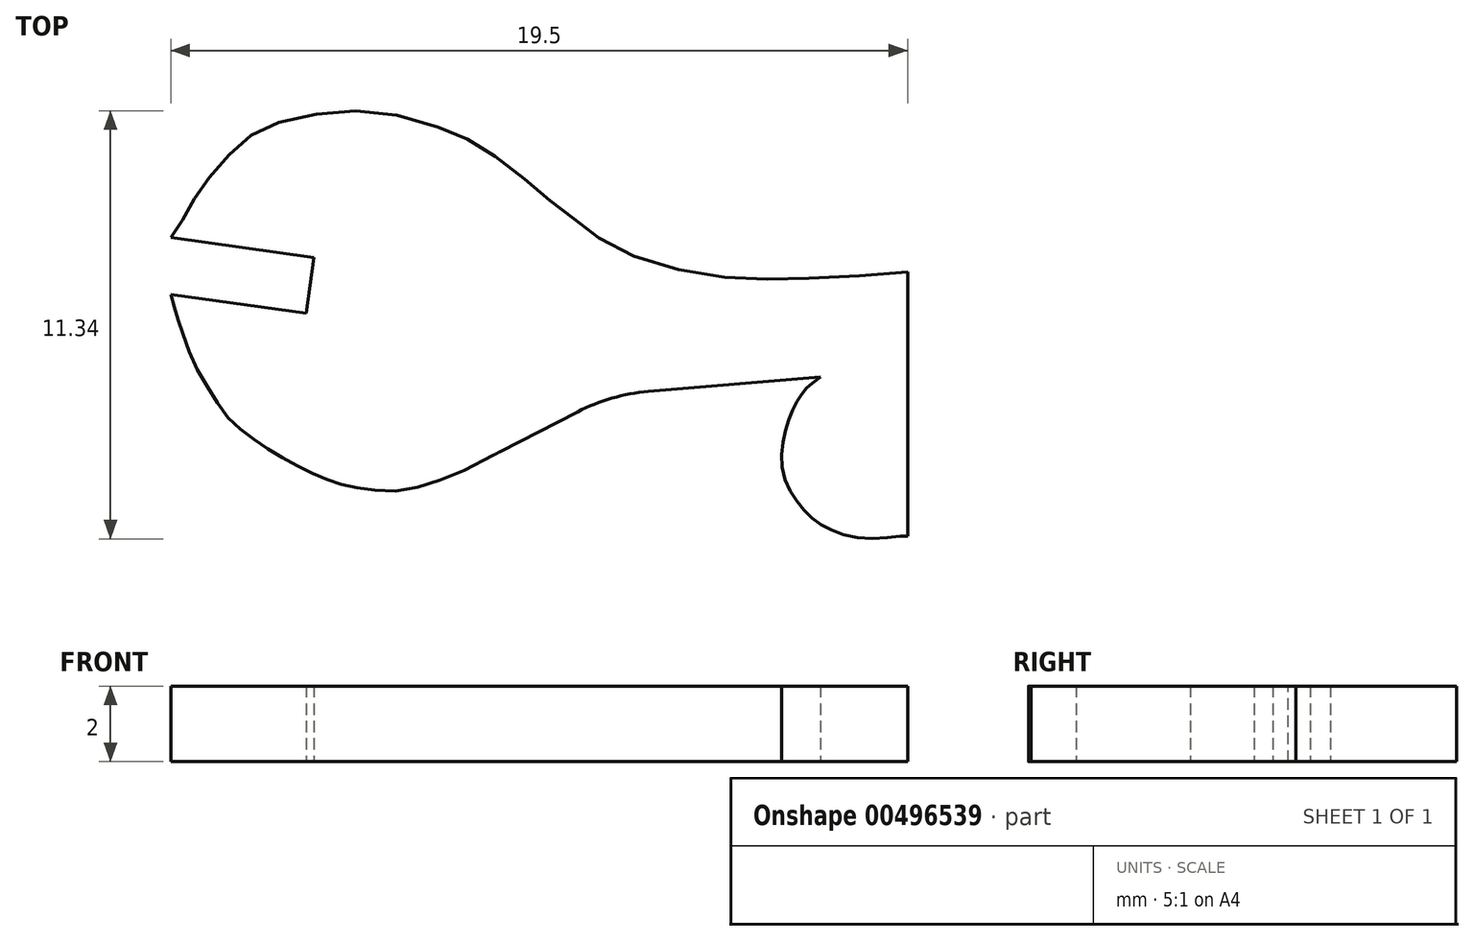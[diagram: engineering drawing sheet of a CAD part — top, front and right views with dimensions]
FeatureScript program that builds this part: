
annotation { "Feature Type Name" : "Feature", "Feature Type Description" : "" }
export const myFeature = defineFeature(function(context is Context, id is Id, definition is map)
    precondition{}
    {
        {
            var Q0;
            Q0=qCreatedBy(makeId("Top.planeOp"),FACE);
            var sketch = newSketch(context, id + "F0", { "sketchPlane" : qUnion([Q0])});
            skLineSegment(sketch, "E0", {"start": v(40.35, 15.47) * mm, "end": v(44.13, 14.94) * mm});
            skLineSegment(sketch, "E1", {"start": v(44.13, 14.94) * mm, "end": v(43.93, 13.45) * mm});
            skLineSegment(sketch, "E2", {"start": v(43.93, 13.45) * mm, "end": v(40.35, 13.96) * mm});
            skFitSpline(sketch, "E3", {"points": [v(40.35, 15.47) * mm, v(40.55, 15.77) * mm, v(40.85, 16.28) * mm, v(41.17, 16.79) * mm, v(41.66, 17.4) * mm, v(42.3, 18.03) * mm, v(43.03, 18.45) * mm, v(44.4, 18.76) * mm, v(45.97, 18.77) * mm, v(47.63, 18.31) * mm, v(48.44, 17.94) * mm, v(49.48, 17.2) * mm, v(50.36, 16.47) * mm, v(51.07, 15.93) * mm, v(51.9, 15.3) * mm, v(53.66, 14.65) * mm, v(55.7, 14.36) * mm, v(57.42, 14.4) * mm, v(59.85, 14.56) * mm], "startDerivative": vector(4.77, 10.8) * mm, "endDerivative": vector(25.03, 3.08) * mm});
            skLineSegment(sketch, "E4", {"start": v(59.85, 14.56) * mm, "end": v(59.85, 7.56) * mm});
            skFitSpline(sketch, "E5", {"points": [v(59.85, 7.56) * mm, v(58.9, 7.48) * mm, v(57.66, 7.8) * mm, v(57.04, 8.33) * mm, v(56.56, 9.24) * mm, v(56.6, 10.28) * mm, v(56.87, 11.02) * mm, v(57.14, 11.43) * mm, v(57.55, 11.76) * mm], "startDerivative": vector(-2.58, 0.6) * mm, "endDerivative": vector(6.42, 4.14) * mm});
            skLineSegment(sketch, "E6", {"start": v(52, 11.3) * mm, "end": v(57.55, 11.76) * mm});
            skFitSpline(sketch, "E7", {"points": [v(40.35, 13.96) * mm, v(40.44, 13.63) * mm, v(40.54, 13.29) * mm, v(40.69, 12.86) * mm, v(40.95, 12.14) * mm, v(41.34, 11.47) * mm, v(41.73, 10.86) * mm, v(42.14, 10.43) * mm, v(42.58, 10.1) * mm, v(43.06, 9.77) * mm, v(43.57, 9.48) * mm, v(44.08, 9.22) * mm, v(44.56, 9.03) * mm, v(44.98, 8.9) * mm, v(45.54, 8.8) * mm, v(46.36, 8.76) * mm, v(47.39, 9) * mm, v(48.96, 9.74) * mm], "startDerivative": vector(2.08, -7.33) * mm, "endDerivative": vector(21.07, 12.06) * mm});
            skLineSegment(sketch, "E8", {"start": v(48.96, 9.74) * mm, "end": v(52, 11.3) * mm});
            skSolve(sketch);
        }
        {
            var Q0;
            Q0 = qSketchRegion(id + "F0", true);
            extrude(context, id + "F1", {"entities" : qUnion([Q0]), "depth" : 2 * mm, "offsetDistance" : 25 * mm});
        }
        {
            var Q0;
            Q0=makeQuery(id+"F1.opExtrude","SWEPT_EDGE",EDGE,{"disambiguationData":[OSD([sQuery(id+"F0.wireOp",EDGE,"E6"),sQuery(id+"F0.wireOp",EDGE,"E8")])]});
            var Q1;
            Q1=makeQuery(id+"F1.opExtrude","SWEPT_EDGE",EDGE,{"disambiguationData":[OSD([sQuery(id+"F0.wireOp",EDGE,"E7"),sQuery(id+"F0.wireOp",EDGE,"E8")])]});
            fillet(context, id + "F2", {"entities" : qUnion([Q0, Q1]), "radius" : 5 * mm, "tangentPropagation" : true, "allowEdgeOverflow" : false});
        }
    });
